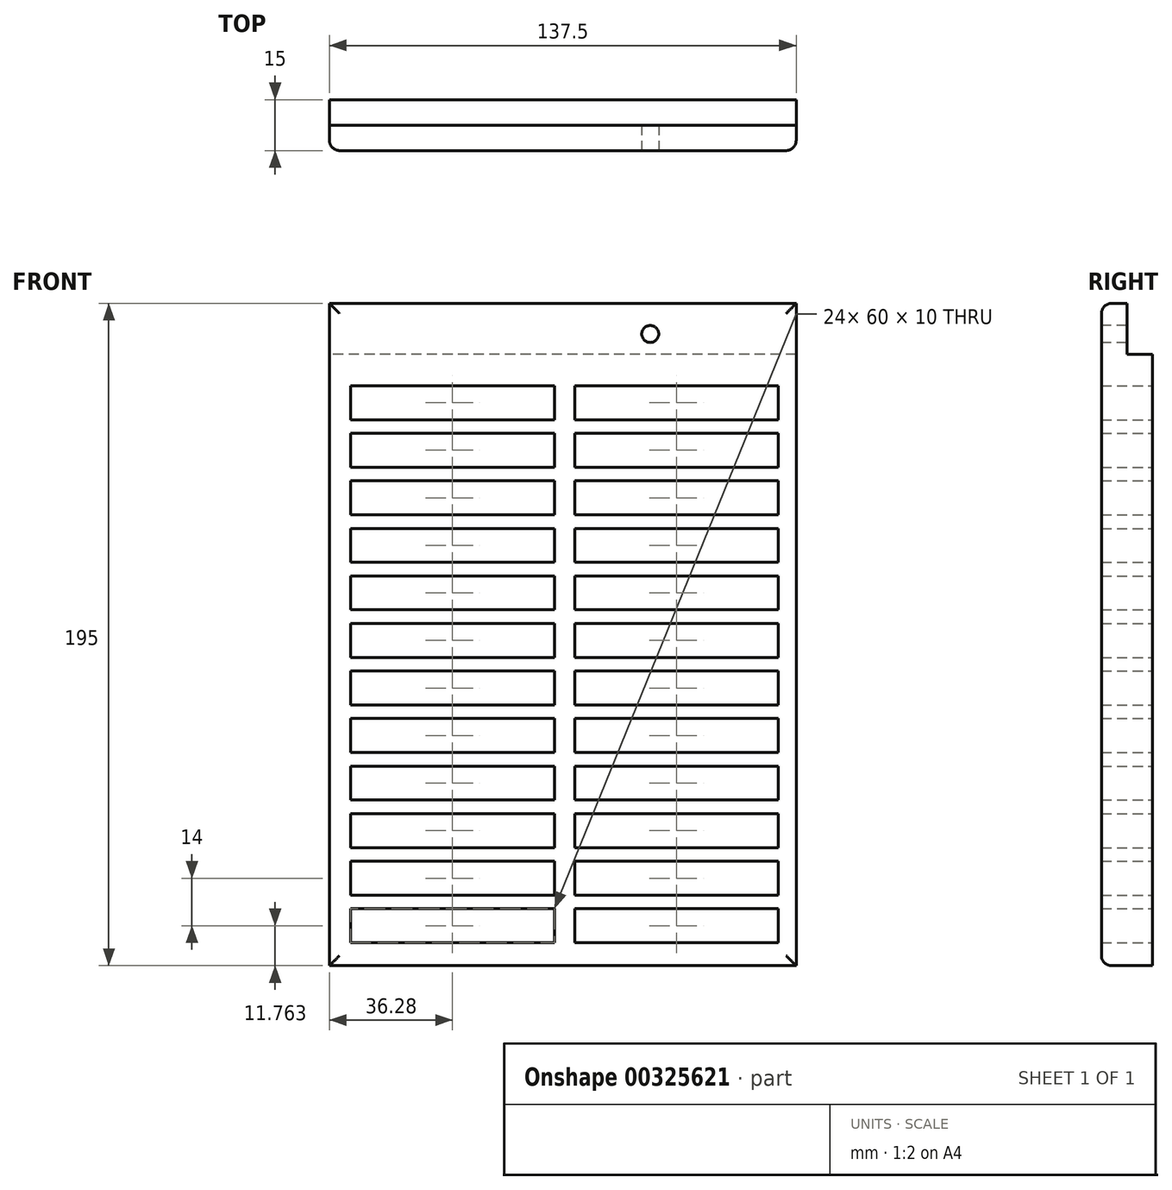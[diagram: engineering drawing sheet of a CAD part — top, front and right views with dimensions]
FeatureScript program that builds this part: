
annotation { "Feature Type Name" : "Feature", "Feature Type Description" : "" }
export const myFeature = defineFeature(function(context is Context, id is Id, definition is map)
    precondition{}
    {
        {
            var Q0;
            Q0=qCreatedBy(makeId("Front.planeOp"),FACE);
            var sketch = newSketch(context, id + "F0", { "sketchPlane" : qUnion([Q0])});
            skLineSegment(sketch, "E0.bottom", {"start": v(-70.3, 100.57) * mm, "end": v(67.2, 100.57) * mm});
            skLineSegment(sketch, "E0.top", {"start": v(-70.3, -94.43) * mm, "end": v(67.2, -94.43) * mm});
            skLineSegment(sketch, "E0.left", {"start": v(-70.3, 100.57) * mm, "end": v(-70.3, -94.43) * mm});
            skLineSegment(sketch, "E0.right", {"start": v(67.2, 100.57) * mm, "end": v(67.2, -94.43) * mm});
            skLineSegment(sketch, "E1.bottom", {"start": v(-64.03, -87.67) * mm, "end": v(-4.03, -87.67) * mm});
            skLineSegment(sketch, "E1.top", {"start": v(-64.03, -77.67) * mm, "end": v(-4.03, -77.67) * mm});
            skLineSegment(sketch, "E1.left", {"start": v(-64.03, -87.67) * mm, "end": v(-64.03, -77.67) * mm});
            skLineSegment(sketch, "E1.right", {"start": v(-4.03, -87.67) * mm, "end": v(-4.03, -77.67) * mm});
            skLineSegment(sketch, "E2.0.1.0", {"start": v(-64.03, -63.67) * mm, "end": v(-4.03, -63.67) * mm});
            skLineSegment(sketch, "E2.0.1.1", {"start": v(-64.03, -73.67) * mm, "end": v(-64.03, -63.67) * mm});
            skLineSegment(sketch, "E2.0.1.2", {"start": v(-64.03, -73.67) * mm, "end": v(-4.03, -73.67) * mm});
            skLineSegment(sketch, "E2.0.1.3", {"start": v(-4.03, -73.67) * mm, "end": v(-4.03, -63.67) * mm});
            skLineSegment(sketch, "E2.0.2.0", {"start": v(-64.03, -49.67) * mm, "end": v(-4.03, -49.67) * mm});
            skLineSegment(sketch, "E2.0.2.1", {"start": v(-64.03, -59.67) * mm, "end": v(-64.03, -49.67) * mm});
            skLineSegment(sketch, "E2.0.2.2", {"start": v(-64.03, -59.67) * mm, "end": v(-4.03, -59.67) * mm});
            skLineSegment(sketch, "E2.0.2.3", {"start": v(-4.03, -59.67) * mm, "end": v(-4.03, -49.67) * mm});
            skLineSegment(sketch, "E2.0.3.0", {"start": v(-64.03, -35.67) * mm, "end": v(-4.03, -35.67) * mm});
            skLineSegment(sketch, "E2.0.3.1", {"start": v(-64.03, -45.67) * mm, "end": v(-64.03, -35.67) * mm});
            skLineSegment(sketch, "E2.0.3.2", {"start": v(-64.03, -45.67) * mm, "end": v(-4.03, -45.67) * mm});
            skLineSegment(sketch, "E2.0.3.3", {"start": v(-4.03, -45.67) * mm, "end": v(-4.03, -35.67) * mm});
            skLineSegment(sketch, "E2.0.4.0", {"start": v(-64.03, -21.67) * mm, "end": v(-4.03, -21.67) * mm});
            skLineSegment(sketch, "E2.0.4.1", {"start": v(-64.03, -31.67) * mm, "end": v(-64.03, -21.67) * mm});
            skLineSegment(sketch, "E2.0.4.2", {"start": v(-64.03, -31.67) * mm, "end": v(-4.03, -31.67) * mm});
            skLineSegment(sketch, "E2.0.4.3", {"start": v(-4.03, -31.67) * mm, "end": v(-4.03, -21.67) * mm});
            skLineSegment(sketch, "E2.0.5.0", {"start": v(-64.03, -7.67) * mm, "end": v(-4.03, -7.67) * mm});
            skLineSegment(sketch, "E2.0.5.1", {"start": v(-64.03, -17.67) * mm, "end": v(-64.03, -7.67) * mm});
            skLineSegment(sketch, "E2.0.5.2", {"start": v(-64.03, -17.67) * mm, "end": v(-4.03, -17.67) * mm});
            skLineSegment(sketch, "E2.0.5.3", {"start": v(-4.03, -17.67) * mm, "end": v(-4.03, -7.67) * mm});
            skLineSegment(sketch, "E2.0.6.0", {"start": v(-64.03, 6.33) * mm, "end": v(-4.03, 6.33) * mm});
            skLineSegment(sketch, "E2.0.6.1", {"start": v(-64.03, -3.67) * mm, "end": v(-64.03, 6.33) * mm});
            skLineSegment(sketch, "E2.0.6.2", {"start": v(-64.03, -3.67) * mm, "end": v(-4.03, -3.67) * mm});
            skLineSegment(sketch, "E2.0.6.3", {"start": v(-4.03, -3.67) * mm, "end": v(-4.03, 6.33) * mm});
            skLineSegment(sketch, "E2.0.7.0", {"start": v(-64.03, 20.33) * mm, "end": v(-4.03, 20.33) * mm});
            skLineSegment(sketch, "E2.0.7.1", {"start": v(-64.03, 10.33) * mm, "end": v(-64.03, 20.33) * mm});
            skLineSegment(sketch, "E2.0.7.2", {"start": v(-64.03, 10.33) * mm, "end": v(-4.03, 10.33) * mm});
            skLineSegment(sketch, "E2.0.7.3", {"start": v(-4.03, 10.33) * mm, "end": v(-4.03, 20.33) * mm});
            skLineSegment(sketch, "E2.0.8.0", {"start": v(-64.03, 34.33) * mm, "end": v(-4.03, 34.33) * mm});
            skLineSegment(sketch, "E2.0.8.1", {"start": v(-64.03, 24.33) * mm, "end": v(-64.03, 34.33) * mm});
            skLineSegment(sketch, "E2.0.8.2", {"start": v(-64.03, 24.33) * mm, "end": v(-4.03, 24.33) * mm});
            skLineSegment(sketch, "E2.0.8.3", {"start": v(-4.03, 24.33) * mm, "end": v(-4.03, 34.33) * mm});
            skLineSegment(sketch, "E2.0.9.0", {"start": v(-64.03, 48.33) * mm, "end": v(-4.03, 48.33) * mm});
            skLineSegment(sketch, "E2.0.9.1", {"start": v(-64.03, 38.33) * mm, "end": v(-64.03, 48.33) * mm});
            skLineSegment(sketch, "E2.0.9.2", {"start": v(-64.03, 38.33) * mm, "end": v(-4.03, 38.33) * mm});
            skLineSegment(sketch, "E2.0.9.3", {"start": v(-4.03, 38.33) * mm, "end": v(-4.03, 48.33) * mm});
            skLineSegment(sketch, "E2.1.0.0", {"start": v(1.97, -77.67) * mm, "end": v(61.97, -77.67) * mm});
            skLineSegment(sketch, "E2.1.0.1", {"start": v(1.97, -87.67) * mm, "end": v(1.97, -77.67) * mm});
            skLineSegment(sketch, "E2.1.0.2", {"start": v(1.97, -87.67) * mm, "end": v(61.97, -87.67) * mm});
            skLineSegment(sketch, "E2.1.0.3", {"start": v(61.97, -87.67) * mm, "end": v(61.97, -77.67) * mm});
            skLineSegment(sketch, "E2.1.1.0", {"start": v(1.97, -63.67) * mm, "end": v(61.97, -63.67) * mm});
            skLineSegment(sketch, "E2.1.1.1", {"start": v(1.97, -73.67) * mm, "end": v(1.97, -63.67) * mm});
            skLineSegment(sketch, "E2.1.1.2", {"start": v(1.97, -73.67) * mm, "end": v(61.97, -73.67) * mm});
            skLineSegment(sketch, "E2.1.1.3", {"start": v(61.97, -73.67) * mm, "end": v(61.97, -63.67) * mm});
            skLineSegment(sketch, "E2.1.2.0", {"start": v(1.97, -49.67) * mm, "end": v(61.97, -49.67) * mm});
            skLineSegment(sketch, "E2.1.2.1", {"start": v(1.97, -59.67) * mm, "end": v(1.97, -49.67) * mm});
            skLineSegment(sketch, "E2.1.2.2", {"start": v(1.97, -59.67) * mm, "end": v(61.97, -59.67) * mm});
            skLineSegment(sketch, "E2.1.2.3", {"start": v(61.97, -59.67) * mm, "end": v(61.97, -49.67) * mm});
            skLineSegment(sketch, "E2.1.3.0", {"start": v(1.97, -35.67) * mm, "end": v(61.97, -35.67) * mm});
            skLineSegment(sketch, "E2.1.3.1", {"start": v(1.97, -45.67) * mm, "end": v(1.97, -35.67) * mm});
            skLineSegment(sketch, "E2.1.3.2", {"start": v(1.97, -45.67) * mm, "end": v(61.97, -45.67) * mm});
            skLineSegment(sketch, "E2.1.3.3", {"start": v(61.97, -45.67) * mm, "end": v(61.97, -35.67) * mm});
            skLineSegment(sketch, "E2.1.4.0", {"start": v(1.97, -21.67) * mm, "end": v(61.97, -21.67) * mm});
            skLineSegment(sketch, "E2.1.4.1", {"start": v(1.97, -31.67) * mm, "end": v(1.97, -21.67) * mm});
            skLineSegment(sketch, "E2.1.4.2", {"start": v(1.97, -31.67) * mm, "end": v(61.97, -31.67) * mm});
            skLineSegment(sketch, "E2.1.4.3", {"start": v(61.97, -31.67) * mm, "end": v(61.97, -21.67) * mm});
            skLineSegment(sketch, "E2.1.5.0", {"start": v(1.97, -7.67) * mm, "end": v(61.97, -7.67) * mm});
            skLineSegment(sketch, "E2.1.5.1", {"start": v(1.97, -17.67) * mm, "end": v(1.97, -7.67) * mm});
            skLineSegment(sketch, "E2.1.5.2", {"start": v(1.97, -17.67) * mm, "end": v(61.97, -17.67) * mm});
            skLineSegment(sketch, "E2.1.5.3", {"start": v(61.97, -17.67) * mm, "end": v(61.97, -7.67) * mm});
            skLineSegment(sketch, "E2.1.6.0", {"start": v(1.97, 6.33) * mm, "end": v(61.97, 6.33) * mm});
            skLineSegment(sketch, "E2.1.6.1", {"start": v(1.97, -3.67) * mm, "end": v(1.97, 6.33) * mm});
            skLineSegment(sketch, "E2.1.6.2", {"start": v(1.97, -3.67) * mm, "end": v(61.97, -3.67) * mm});
            skLineSegment(sketch, "E2.1.6.3", {"start": v(61.97, -3.67) * mm, "end": v(61.97, 6.33) * mm});
            skLineSegment(sketch, "E2.1.7.0", {"start": v(1.97, 20.33) * mm, "end": v(61.97, 20.33) * mm});
            skLineSegment(sketch, "E2.1.7.1", {"start": v(1.97, 10.33) * mm, "end": v(1.97, 20.33) * mm});
            skLineSegment(sketch, "E2.1.7.2", {"start": v(1.97, 10.33) * mm, "end": v(61.97, 10.33) * mm});
            skLineSegment(sketch, "E2.1.7.3", {"start": v(61.97, 10.33) * mm, "end": v(61.97, 20.33) * mm});
            skLineSegment(sketch, "E2.1.8.0", {"start": v(1.97, 34.33) * mm, "end": v(61.97, 34.33) * mm});
            skLineSegment(sketch, "E2.1.8.1", {"start": v(1.97, 24.33) * mm, "end": v(1.97, 34.33) * mm});
            skLineSegment(sketch, "E2.1.8.2", {"start": v(1.97, 24.33) * mm, "end": v(61.97, 24.33) * mm});
            skLineSegment(sketch, "E2.1.8.3", {"start": v(61.97, 24.33) * mm, "end": v(61.97, 34.33) * mm});
            skLineSegment(sketch, "E2.1.9.0", {"start": v(1.97, 48.33) * mm, "end": v(61.97, 48.33) * mm});
            skLineSegment(sketch, "E2.1.9.1", {"start": v(1.97, 38.33) * mm, "end": v(1.97, 48.33) * mm});
            skLineSegment(sketch, "E2.1.9.2", {"start": v(1.97, 38.33) * mm, "end": v(61.97, 38.33) * mm});
            skLineSegment(sketch, "E2.1.9.3", {"start": v(61.97, 38.33) * mm, "end": v(61.97, 48.33) * mm});
            skLineSegment(sketch, "E2.direction1", {"start": v(-64.03, -87.67) * mm, "end": v(1.97, -87.67) * mm, "construction": true});
            skLineSegment(sketch, "E2.direction2", {"start": v(-64.03, -87.67) * mm, "end": v(-64.03, -73.67) * mm, "construction": true});
            skLineSegment(sketch, "E3.0.0.10", {"start": v(-64.03, 62.33) * mm, "end": v(-4.03, 62.33) * mm});
            skLineSegment(sketch, "E3.3.0.10", {"start": v(-64.03, 52.33) * mm, "end": v(-64.03, 62.33) * mm});
            skLineSegment(sketch, "E3.6.0.10", {"start": v(-64.03, 52.33) * mm, "end": v(-4.03, 52.33) * mm});
            skLineSegment(sketch, "E3.9.0.10", {"start": v(-4.03, 52.33) * mm, "end": v(-4.03, 62.33) * mm});
            skLineSegment(sketch, "E3.0.0.11", {"start": v(-64.03, 76.33) * mm, "end": v(-4.03, 76.33) * mm});
            skLineSegment(sketch, "E3.3.0.11", {"start": v(-64.03, 66.33) * mm, "end": v(-64.03, 76.33) * mm});
            skLineSegment(sketch, "E3.6.0.11", {"start": v(-64.03, 66.33) * mm, "end": v(-4.03, 66.33) * mm});
            skLineSegment(sketch, "E3.9.0.11", {"start": v(-4.03, 66.33) * mm, "end": v(-4.03, 76.33) * mm});
            skLineSegment(sketch, "E3.0.1.10", {"start": v(1.97, 62.33) * mm, "end": v(61.97, 62.33) * mm});
            skLineSegment(sketch, "E3.3.1.10", {"start": v(1.97, 52.33) * mm, "end": v(1.97, 62.33) * mm});
            skLineSegment(sketch, "E3.6.1.10", {"start": v(1.97, 52.33) * mm, "end": v(61.97, 52.33) * mm});
            skLineSegment(sketch, "E3.9.1.10", {"start": v(61.97, 52.33) * mm, "end": v(61.97, 62.33) * mm});
            skLineSegment(sketch, "E3.0.1.11", {"start": v(1.97, 76.33) * mm, "end": v(61.97, 76.33) * mm});
            skLineSegment(sketch, "E3.3.1.11", {"start": v(1.97, 66.33) * mm, "end": v(1.97, 76.33) * mm});
            skLineSegment(sketch, "E3.6.1.11", {"start": v(1.97, 66.33) * mm, "end": v(61.97, 66.33) * mm});
            skLineSegment(sketch, "E3.9.1.11", {"start": v(61.97, 66.33) * mm, "end": v(61.97, 76.33) * mm});
            skSolve(sketch);
        }
        {
            var Q0;
            Q0=makeQuery(id+"F0.imprint","IMPRINT",FACE,{"disambiguationData":[TD([[makeQuery(id+"F0.imprint","IMPRINT",EDGE,{"derivedFrom":sQuery(id+"F0.wireOp",EDGE,"E0.bottom")}),-1.0]])]});
            extrude(context, id + "F1", {"entities" : qUnion([Q0]), "depth" : 15 * mm});
        }
        {
            var Q0;
            Q0=qCreatedBy(makeId("Front.planeOp"),FACE);
            var sketch = newSketch(context, id + "F2", { "sketchPlane" : qUnion([Q0])});
            skLineSegment(sketch, "E4.bottom", {"start": v(67.2, 100.57) * mm, "end": v(-70.3, 100.57) * mm});
            skLineSegment(sketch, "E4.top", {"start": v(67.2, 85.57) * mm, "end": v(-70.3, 85.57) * mm});
            skLineSegment(sketch, "E4.left", {"start": v(67.2, 100.57) * mm, "end": v(67.2, 85.57) * mm});
            skLineSegment(sketch, "E4.right", {"start": v(-70.3, 100.57) * mm, "end": v(-70.3, 85.57) * mm});
            skSolve(sketch);
        }
        {
            var Q0;
            Q0=makeQuery(id+"F2.imprint","IMPRINT",FACE,{"disambiguationData":[TD([[makeQuery(id+"F2.imprint","IMPRINT",EDGE,{"derivedFrom":sQuery(id+"F2.wireOp",EDGE,"E4.bottom")}),1.0]])]});
            extrude(context, id + "F3", {"entities" : qUnion([Q0]), "operationType" : NewBodyOperationType.REMOVE, "depth" : 7.5 * mm});
        }
        {
            var Q0;
            Q0=makeQuery(id+"F1.opExtrude","CAP_FACE",FACE,{"disambiguationData":[OSD([sQuery(id+"F0.wireOp",EDGE,"E0.bottom"),sQuery(id+"F0.wireOp",EDGE,"E0.top"),sQuery(id+"F0.wireOp",EDGE,"E0.left"),sQuery(id+"F0.wireOp",EDGE,"E0.right"),sQuery(id+"F0.wireOp",EDGE,"E1.bottom"),sQuery(id+"F0.wireOp",EDGE,"E1.top"),sQuery(id+"F0.wireOp",EDGE,"E1.left"),sQuery(id+"F0.wireOp",EDGE,"E1.right"),sQuery(id+"F0.wireOp",EDGE,"E2.0.1.0"),sQuery(id+"F0.wireOp",EDGE,"E2.0.1.1"),sQuery(id+"F0.wireOp",EDGE,"E2.0.1.2"),sQuery(id+"F0.wireOp",EDGE,"E2.0.1.3"),sQuery(id+"F0.wireOp",EDGE,"E2.0.2.0"),sQuery(id+"F0.wireOp",EDGE,"E2.0.2.1"),sQuery(id+"F0.wireOp",EDGE,"E2.0.2.2"),sQuery(id+"F0.wireOp",EDGE,"E2.0.2.3"),sQuery(id+"F0.wireOp",EDGE,"E2.0.3.0"),sQuery(id+"F0.wireOp",EDGE,"E2.0.3.1"),sQuery(id+"F0.wireOp",EDGE,"E2.0.3.2"),sQuery(id+"F0.wireOp",EDGE,"E2.0.3.3"),sQuery(id+"F0.wireOp",EDGE,"E2.0.4.0"),sQuery(id+"F0.wireOp",EDGE,"E2.0.4.1"),sQuery(id+"F0.wireOp",EDGE,"E2.0.4.2"),sQuery(id+"F0.wireOp",EDGE,"E2.0.4.3"),sQuery(id+"F0.wireOp",EDGE,"E2.0.5.0"),sQuery(id+"F0.wireOp",EDGE,"E2.0.5.1"),sQuery(id+"F0.wireOp",EDGE,"E2.0.5.2"),sQuery(id+"F0.wireOp",EDGE,"E2.0.5.3"),sQuery(id+"F0.wireOp",EDGE,"E2.0.6.0"),sQuery(id+"F0.wireOp",EDGE,"E2.0.6.1"),sQuery(id+"F0.wireOp",EDGE,"E2.0.6.2"),sQuery(id+"F0.wireOp",EDGE,"E2.0.6.3"),sQuery(id+"F0.wireOp",EDGE,"E2.0.7.0"),sQuery(id+"F0.wireOp",EDGE,"E2.0.7.1"),sQuery(id+"F0.wireOp",EDGE,"E2.0.7.2"),sQuery(id+"F0.wireOp",EDGE,"E2.0.7.3"),sQuery(id+"F0.wireOp",EDGE,"E2.0.8.0"),sQuery(id+"F0.wireOp",EDGE,"E2.0.8.1"),sQuery(id+"F0.wireOp",EDGE,"E2.0.8.2"),sQuery(id+"F0.wireOp",EDGE,"E2.0.8.3"),sQuery(id+"F0.wireOp",EDGE,"E2.0.9.0"),sQuery(id+"F0.wireOp",EDGE,"E2.0.9.1"),sQuery(id+"F0.wireOp",EDGE,"E2.0.9.2"),sQuery(id+"F0.wireOp",EDGE,"E2.0.9.3"),sQuery(id+"F0.wireOp",EDGE,"E2.1.0.0"),sQuery(id+"F0.wireOp",EDGE,"E2.1.0.1"),sQuery(id+"F0.wireOp",EDGE,"E2.1.0.2"),sQuery(id+"F0.wireOp",EDGE,"E2.1.0.3"),sQuery(id+"F0.wireOp",EDGE,"E2.1.1.0"),sQuery(id+"F0.wireOp",EDGE,"E2.1.1.1"),sQuery(id+"F0.wireOp",EDGE,"E2.1.1.2"),sQuery(id+"F0.wireOp",EDGE,"E2.1.1.3"),sQuery(id+"F0.wireOp",EDGE,"E2.1.2.0"),sQuery(id+"F0.wireOp",EDGE,"E2.1.2.1"),sQuery(id+"F0.wireOp",EDGE,"E2.1.2.2"),sQuery(id+"F0.wireOp",EDGE,"E2.1.2.3"),sQuery(id+"F0.wireOp",EDGE,"E2.1.3.0"),sQuery(id+"F0.wireOp",EDGE,"E2.1.3.1"),sQuery(id+"F0.wireOp",EDGE,"E2.1.3.2"),sQuery(id+"F0.wireOp",EDGE,"E2.1.3.3"),sQuery(id+"F0.wireOp",EDGE,"E2.1.4.0"),sQuery(id+"F0.wireOp",EDGE,"E2.1.4.1"),sQuery(id+"F0.wireOp",EDGE,"E2.1.4.2"),sQuery(id+"F0.wireOp",EDGE,"E2.1.4.3"),sQuery(id+"F0.wireOp",EDGE,"E2.1.5.0"),sQuery(id+"F0.wireOp",EDGE,"E2.1.5.1"),sQuery(id+"F0.wireOp",EDGE,"E2.1.5.2"),sQuery(id+"F0.wireOp",EDGE,"E2.1.5.3"),sQuery(id+"F0.wireOp",EDGE,"E2.1.6.0"),sQuery(id+"F0.wireOp",EDGE,"E2.1.6.1"),sQuery(id+"F0.wireOp",EDGE,"E2.1.6.2"),sQuery(id+"F0.wireOp",EDGE,"E2.1.6.3"),sQuery(id+"F0.wireOp",EDGE,"E2.1.7.0"),sQuery(id+"F0.wireOp",EDGE,"E2.1.7.1"),sQuery(id+"F0.wireOp",EDGE,"E2.1.7.2"),sQuery(id+"F0.wireOp",EDGE,"E2.1.7.3"),sQuery(id+"F0.wireOp",EDGE,"E2.1.8.0"),sQuery(id+"F0.wireOp",EDGE,"E2.1.8.1"),sQuery(id+"F0.wireOp",EDGE,"E2.1.8.2"),sQuery(id+"F0.wireOp",EDGE,"E2.1.8.3"),sQuery(id+"F0.wireOp",EDGE,"E2.1.9.0"),sQuery(id+"F0.wireOp",EDGE,"E2.1.9.1"),sQuery(id+"F0.wireOp",EDGE,"E2.1.9.2"),sQuery(id+"F0.wireOp",EDGE,"E2.1.9.3"),sQuery(id+"F0.wireOp",EDGE,"E3.0.0.10"),sQuery(id+"F0.wireOp",EDGE,"E3.3.0.10"),sQuery(id+"F0.wireOp",EDGE,"E3.6.0.10"),sQuery(id+"F0.wireOp",EDGE,"E3.9.0.10"),sQuery(id+"F0.wireOp",EDGE,"E3.0.0.11"),sQuery(id+"F0.wireOp",EDGE,"E3.3.0.11"),sQuery(id+"F0.wireOp",EDGE,"E3.6.0.11"),sQuery(id+"F0.wireOp",EDGE,"E3.9.0.11"),sQuery(id+"F0.wireOp",EDGE,"E3.0.1.10"),sQuery(id+"F0.wireOp",EDGE,"E3.3.1.10"),sQuery(id+"F0.wireOp",EDGE,"E3.6.1.10"),sQuery(id+"F0.wireOp",EDGE,"E3.9.1.10"),sQuery(id+"F0.wireOp",EDGE,"E3.0.1.11"),sQuery(id+"F0.wireOp",EDGE,"E3.3.1.11"),sQuery(id+"F0.wireOp",EDGE,"E3.6.1.11"),sQuery(id+"F0.wireOp",EDGE,"E3.9.1.11")])],"isStart":false});
            var sketch = newSketch(context, id + "F4", { "sketchPlane" : qUnion([Q0])});
            skCircle(sketch, "E5", {"center": v(24.2, 91.57) * mm, "radius": 2.5 * mm});
            skSolve(sketch);
        }
        {
            var Q0;
            Q0=makeQuery(id+"F4.imprint","IMPRINT",FACE,{"disambiguationData":[TD([[makeQuery(id+"F4.imprint","IMPRINT",EDGE,{"derivedFrom":sQuery(id+"F4.wireOp",EDGE,"E5")}),1.0]])]});
            extrude(context, id + "F5", {"entities" : qUnion([Q0]), "operationType" : NewBodyOperationType.REMOVE, "endBound" : BoundingType.UP_TO_NEXT, "oppositeDirection" : true, "depth" : 25 * mm});
        }
        {
            var Q0;
            Q0=makeQuery(id+"F1.opExtrude","CAP_EDGE",EDGE,{"disambiguationData":[OSD([sQuery(id+"F0.wireOp",EDGE,"E0.bottom")])],"isStart":false});
            var Q1;
            Q1=makeQuery(id+"F1.opExtrude","CAP_EDGE",EDGE,{"disambiguationData":[OSD([sQuery(id+"F0.wireOp",EDGE,"E0.left")])],"isStart":false});
            var Q2;
            Q2=makeQuery(id+"F1.opExtrude","CAP_EDGE",EDGE,{"disambiguationData":[OSD([sQuery(id+"F0.wireOp",EDGE,"E0.right")])],"isStart":false});
            var Q3;
            Q3=makeQuery(id+"F1.opExtrude","CAP_EDGE",EDGE,{"disambiguationData":[OSD([sQuery(id+"F0.wireOp",EDGE,"E0.top")])],"isStart":false});
            fillet(context, id + "F6", {"entities" : qUnion([Q0, Q1, Q2, Q3]), "radius" : 3 * mm, "tangentPropagation" : true, "allowEdgeOverflow" : false});
        }
    });
